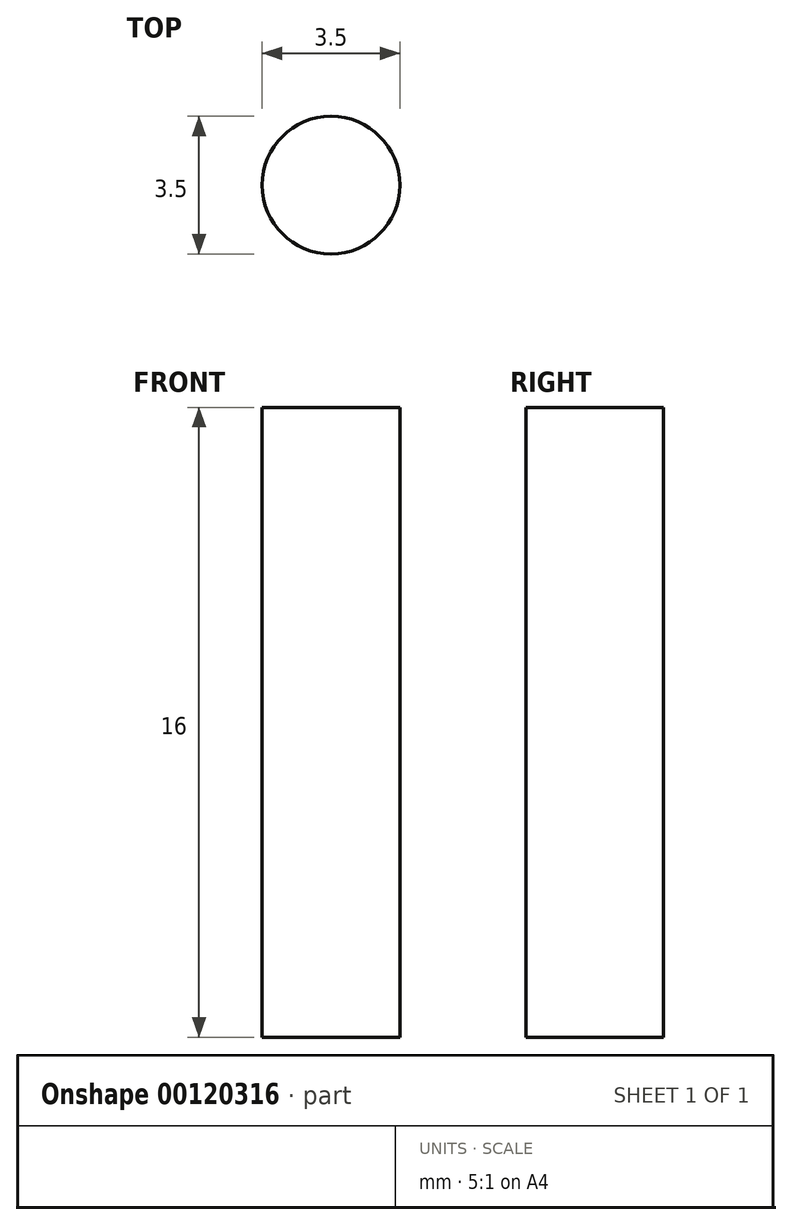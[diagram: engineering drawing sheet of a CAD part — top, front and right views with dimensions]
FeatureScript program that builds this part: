
annotation { "Feature Type Name" : "Feature", "Feature Type Description" : "" }
export const myFeature = defineFeature(function(context is Context, id is Id, definition is map)
    precondition{}
    {
        {
            var Q0;
            Q0=qCreatedBy(makeId("Top.planeOp"),FACE);
            var sketch = newSketch(context, id + "F0", { "sketchPlane" : qUnion([Q0])});
            skCircle(sketch, "E0", {"center": v(0, 0) * mm, "radius": 1.75 * mm});
            skSolve(sketch);
        }
        {
            var Q0;
            Q0 = qSketchRegion(id + "F0", true);
            extrude(context, id + "F1", {"entities" : qUnion([Q0]), "depth" : 16 * mm});
        }
    });
